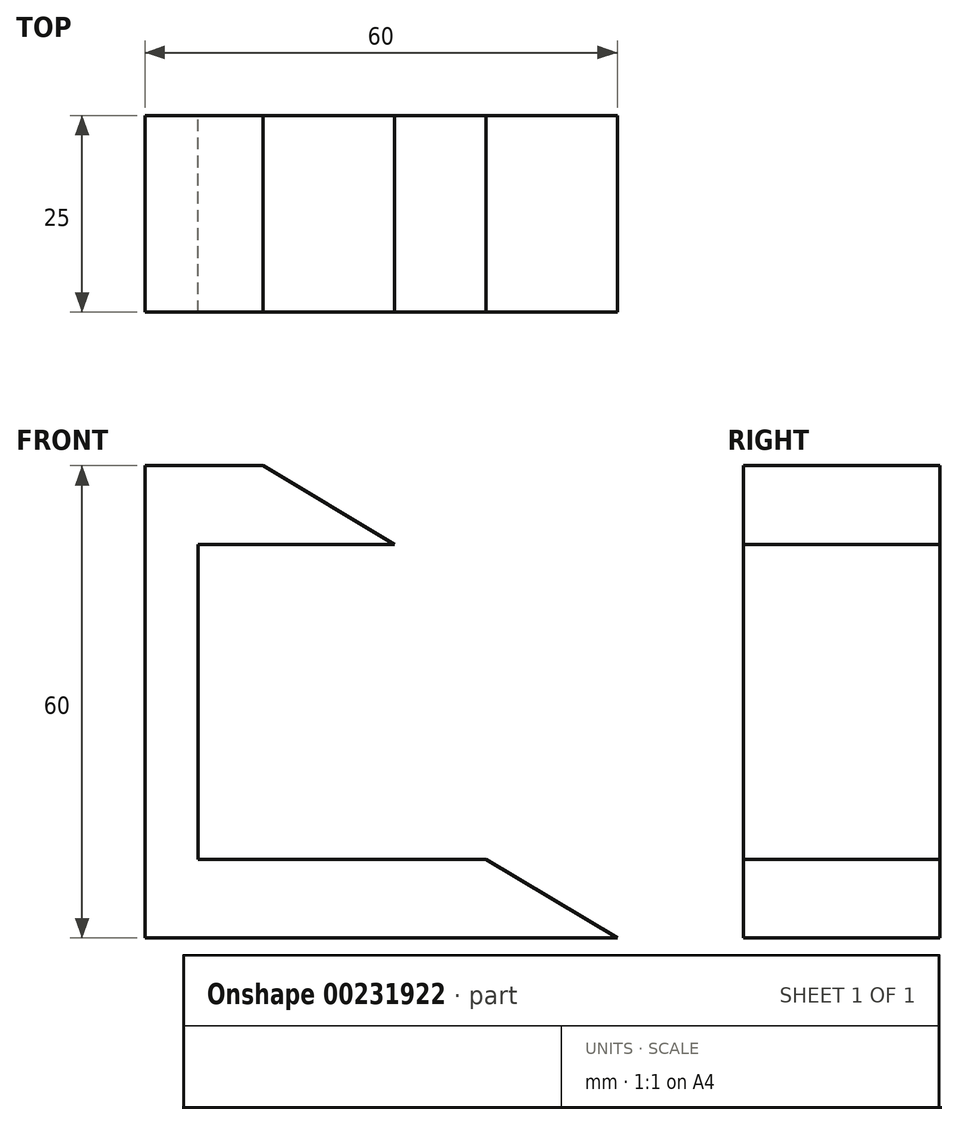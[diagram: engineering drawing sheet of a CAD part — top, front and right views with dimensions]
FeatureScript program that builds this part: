
annotation { "Feature Type Name" : "Feature", "Feature Type Description" : "" }
export const myFeature = defineFeature(function(context is Context, id is Id, definition is map)
    precondition{}
    {
        {
            var Q0;
            Q0=qCreatedBy(makeId("Front.planeOp"),FACE);
            var sketch = newSketch(context, id + "F0", { "sketchPlane" : qUnion([Q0])});
            skLineSegment(sketch, "E0", {"start": v(-44.8, 76.37) * mm, "end": v(-59.8, 76.37) * mm});
            skLineSegment(sketch, "E1", {"start": v(-59.8, 76.37) * mm, "end": v(-59.8, 16.37) * mm});
            skLineSegment(sketch, "E2", {"start": v(-59.8, 16.37) * mm, "end": v(0.2, 16.37) * mm});
            skLineSegment(sketch, "E3", {"start": v(-44.8, 76.37) * mm, "end": v(-28.12, 66.37) * mm});
            skLineSegment(sketch, "E4", {"start": v(-53.1, 66.37) * mm, "end": v(-53.1, 26.37) * mm});
            skLineSegment(sketch, "E5", {"start": v(-53.1, 26.37) * mm, "end": v(-16.49, 26.37) * mm});
            skLineSegment(sketch, "E6", {"start": v(-16.49, 26.37) * mm, "end": v(0.2, 16.37) * mm});
            skLineSegment(sketch, "E7", {"start": v(-28.12, 66.37) * mm, "end": v(-53.1, 66.37) * mm});
            skSolve(sketch);
        }
        {
            var Q0;
            Q0=makeQuery(id+"F0.imprint","IMPRINT",FACE,{"disambiguationData":[TD([[makeQuery(id+"F0.imprint","IMPRINT",EDGE,{"derivedFrom":sQuery(id+"F0.wireOp",EDGE,"E0")}),1.0]])]});
            extrude(context, id + "F1", {"entities" : qUnion([Q0]), "depth" : 25 * mm});
        }
    });
